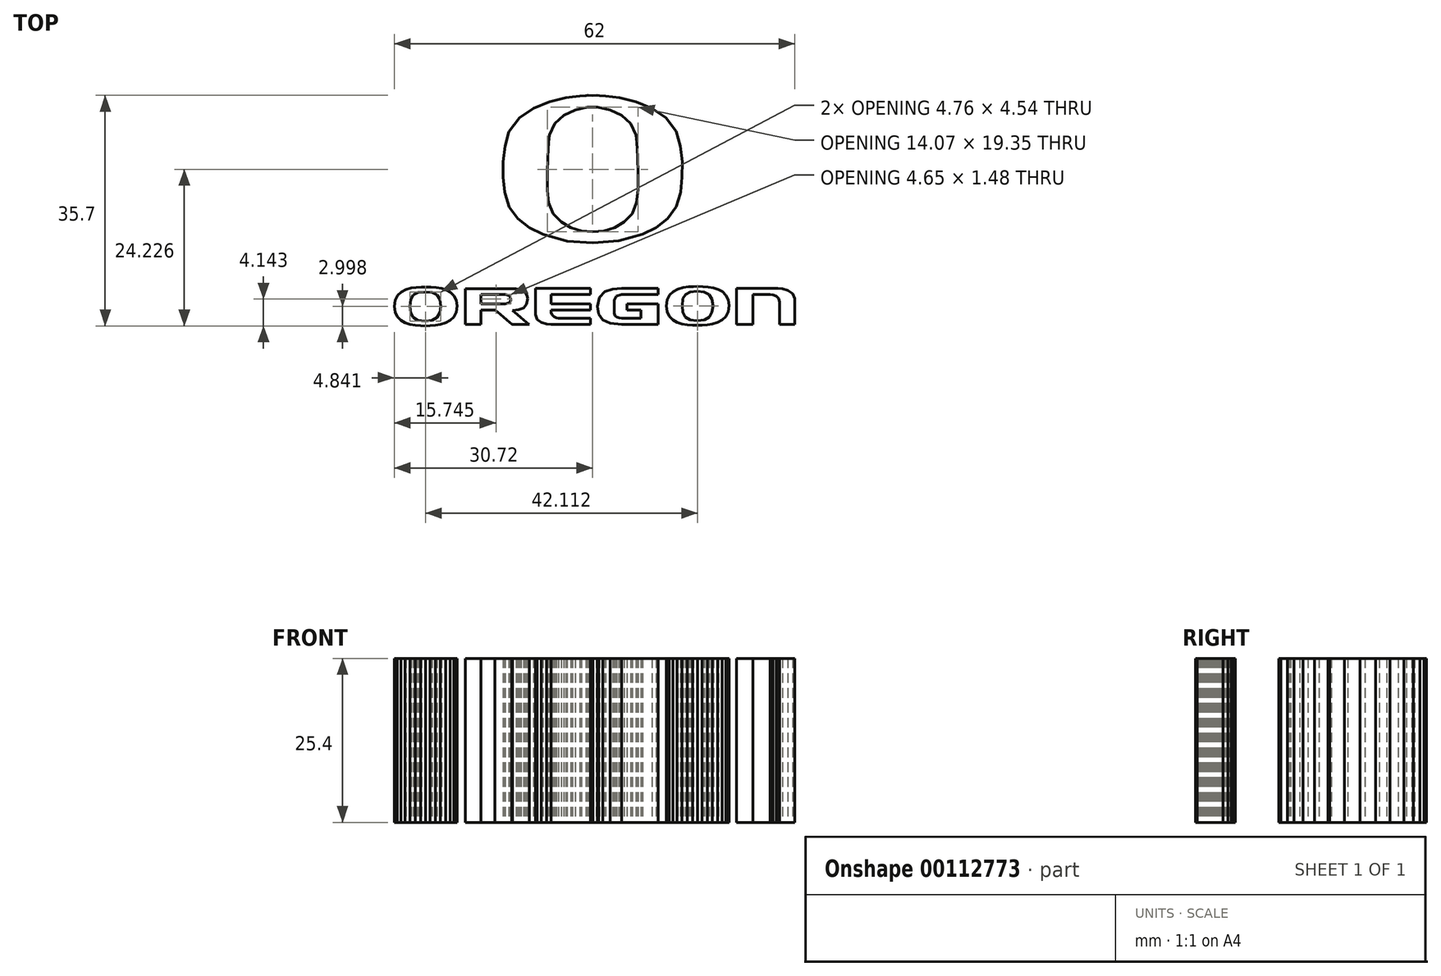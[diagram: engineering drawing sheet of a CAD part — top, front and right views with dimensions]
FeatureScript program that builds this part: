
annotation { "Feature Type Name" : "Feature", "Feature Type Description" : "" }
export const myFeature = defineFeature(function(context is Context, id is Id, definition is map)
    precondition{}
    {
        {
            var Q0;
            Q0=qCreatedBy(makeId("Top.planeOp"),FACE);
            var sketch = newSketch(context, id + "F0", { "sketchPlane" : qUnion([Q0])});
            skLineSegment(sketch, "E0", {"start": v(20.84, -14.7) * mm, "end": v(20.7, -15.65) * mm});
            skLineSegment(sketch, "E1", {"start": v(20.7, -15.65) * mm, "end": v(20.32, -16.38) * mm});
            skLineSegment(sketch, "E2", {"start": v(20.32, -16.38) * mm, "end": v(19.75, -16.93) * mm});
            skLineSegment(sketch, "E3", {"start": v(19.75, -16.93) * mm, "end": v(19.04, -17.3) * mm});
            skLineSegment(sketch, "E4", {"start": v(19.04, -17.3) * mm, "end": v(18.26, -17.56) * mm});
            skLineSegment(sketch, "E5", {"start": v(18.26, -17.56) * mm, "end": v(17.45, -17.7) * mm});
            skLineSegment(sketch, "E6", {"start": v(17.45, -17.7) * mm, "end": v(16.67, -17.76) * mm});
            skLineSegment(sketch, "E7", {"start": v(16.67, -17.76) * mm, "end": v(15.98, -17.78) * mm});
            skLineSegment(sketch, "E8", {"start": v(15.98, -17.78) * mm, "end": v(15.19, -17.76) * mm});
            skLineSegment(sketch, "E9", {"start": v(15.19, -17.76) * mm, "end": v(14.36, -17.68) * mm});
            skLineSegment(sketch, "E10", {"start": v(14.36, -17.68) * mm, "end": v(13.55, -17.53) * mm});
            skLineSegment(sketch, "E11", {"start": v(13.55, -17.53) * mm, "end": v(12.79, -17.28) * mm});
            skLineSegment(sketch, "E12", {"start": v(12.79, -17.28) * mm, "end": v(12.12, -16.9) * mm});
            skLineSegment(sketch, "E13", {"start": v(12.12, -16.9) * mm, "end": v(11.59, -16.36) * mm});
            skLineSegment(sketch, "E14", {"start": v(11.59, -16.36) * mm, "end": v(11.24, -15.66) * mm});
            skLineSegment(sketch, "E15", {"start": v(11.24, -15.66) * mm, "end": v(11.11, -14.76) * mm});
            skLineSegment(sketch, "E16", {"start": v(11.11, -14.76) * mm, "end": v(11.25, -13.79) * mm});
            skLineSegment(sketch, "E17", {"start": v(11.25, -13.79) * mm, "end": v(11.63, -13.05) * mm});
            skLineSegment(sketch, "E18", {"start": v(11.63, -13.05) * mm, "end": v(12.2, -12.52) * mm});
            skLineSegment(sketch, "E19", {"start": v(12.2, -12.52) * mm, "end": v(12.92, -12.15) * mm});
            skLineSegment(sketch, "E20", {"start": v(12.92, -12.15) * mm, "end": v(13.7, -11.92) * mm});
            skLineSegment(sketch, "E21", {"start": v(13.7, -11.92) * mm, "end": v(14.53, -11.8) * mm});
            skLineSegment(sketch, "E22", {"start": v(14.53, -11.8) * mm, "end": v(15.32, -11.75) * mm});
            skLineSegment(sketch, "E23", {"start": v(15.32, -11.75) * mm, "end": v(16.04, -11.74) * mm});
            skLineSegment(sketch, "E24", {"start": v(16.04, -11.74) * mm, "end": v(16.8, -11.76) * mm});
            skLineSegment(sketch, "E25", {"start": v(16.8, -11.76) * mm, "end": v(17.6, -11.82) * mm});
            skLineSegment(sketch, "E26", {"start": v(17.6, -11.82) * mm, "end": v(18.4, -11.96) * mm});
            skLineSegment(sketch, "E27", {"start": v(18.4, -11.96) * mm, "end": v(19.16, -12.2) * mm});
            skLineSegment(sketch, "E28", {"start": v(19.16, -12.2) * mm, "end": v(19.83, -12.56) * mm});
            skLineSegment(sketch, "E29", {"start": v(19.83, -12.56) * mm, "end": v(20.36, -13.08) * mm});
            skLineSegment(sketch, "E30", {"start": v(20.36, -13.08) * mm, "end": v(20.71, -13.79) * mm});
            skLineSegment(sketch, "E31", {"start": v(20.71, -13.79) * mm, "end": v(20.84, -14.7) * mm});
            skLineSegment(sketch, "E32", {"start": v(-0.63, -12.05) * mm, "end": v(-0.63, -12.97) * mm});
            skLineSegment(sketch, "E33", {"start": v(-0.63, -12.97) * mm, "end": v(-6.73, -12.97) * mm});
            skLineSegment(sketch, "E34", {"start": v(-6.73, -12.97) * mm, "end": v(-6.73, -13.2) * mm});
            skLineSegment(sketch, "E35", {"start": v(-6.73, -13.2) * mm, "end": v(-6.73, -13.7) * mm});
            skLineSegment(sketch, "E36", {"start": v(-6.73, -13.7) * mm, "end": v(-6.73, -14.21) * mm});
            skLineSegment(sketch, "E37", {"start": v(-6.73, -14.21) * mm, "end": v(-6.73, -14.45) * mm});
            skLineSegment(sketch, "E38", {"start": v(-6.73, -14.45) * mm, "end": v(-0.63, -14.45) * mm});
            skLineSegment(sketch, "E39", {"start": v(-0.63, -14.45) * mm, "end": v(-0.63, -15.37) * mm});
            skLineSegment(sketch, "E40", {"start": v(-0.63, -15.37) * mm, "end": v(-6.73, -15.37) * mm});
            skLineSegment(sketch, "E41", {"start": v(-6.73, -15.37) * mm, "end": v(-6.74, -15.56) * mm});
            skLineSegment(sketch, "E42", {"start": v(-6.74, -15.56) * mm, "end": v(-6.74, -15.77) * mm});
            skLineSegment(sketch, "E43", {"start": v(-6.74, -15.77) * mm, "end": v(-6.6, -16.1) * mm});
            skLineSegment(sketch, "E44", {"start": v(-6.6, -16.1) * mm, "end": v(-6.27, -16.4) * mm});
            skLineSegment(sketch, "E45", {"start": v(-6.27, -16.4) * mm, "end": v(-5.87, -16.6) * mm});
            skLineSegment(sketch, "E46", {"start": v(-5.87, -16.6) * mm, "end": v(-5.55, -16.67) * mm});
            skLineSegment(sketch, "E47", {"start": v(-5.55, -16.67) * mm, "end": v(-0.63, -16.67) * mm});
            skLineSegment(sketch, "E48", {"start": v(-0.63, -16.67) * mm, "end": v(-0.63, -17.65) * mm});
            skLineSegment(sketch, "E49", {"start": v(-0.63, -17.65) * mm, "end": v(-6.73, -17.65) * mm});
            skLineSegment(sketch, "E50", {"start": v(-6.73, -17.65) * mm, "end": v(-7.45, -17.58) * mm});
            skLineSegment(sketch, "E51", {"start": v(-7.45, -17.58) * mm, "end": v(-8.23, -17.33) * mm});
            skLineSegment(sketch, "E52", {"start": v(-8.23, -17.33) * mm, "end": v(-8.87, -16.85) * mm});
            skLineSegment(sketch, "E53", {"start": v(-8.87, -16.85) * mm, "end": v(-9.13, -16.07) * mm});
            skLineSegment(sketch, "E54", {"start": v(-9.13, -16.07) * mm, "end": v(-9.13, -12.05) * mm});
            skLineSegment(sketch, "E55", {"start": v(-9.13, -12.05) * mm, "end": v(-0.63, -12.05) * mm});
            skLineSegment(sketch, "E56", {"start": v(9.82, -12.05) * mm, "end": v(9.82, -12.97) * mm});
            skLineSegment(sketch, "E57", {"start": v(9.82, -12.97) * mm, "end": v(4.17, -12.97) * mm});
            skLineSegment(sketch, "E58", {"start": v(4.17, -12.97) * mm, "end": v(3.37, -13.2) * mm});
            skLineSegment(sketch, "E59", {"start": v(3.37, -13.2) * mm, "end": v(3.06, -13.9) * mm});
            skLineSegment(sketch, "E60", {"start": v(3.06, -13.9) * mm, "end": v(3.06, -15.9) * mm});
            skLineSegment(sketch, "E61", {"start": v(3.06, -15.9) * mm, "end": v(3.17, -16.27) * mm});
            skLineSegment(sketch, "E62", {"start": v(3.17, -16.27) * mm, "end": v(3.44, -16.5) * mm});
            skLineSegment(sketch, "E63", {"start": v(3.44, -16.5) * mm, "end": v(3.8, -16.63) * mm});
            skLineSegment(sketch, "E64", {"start": v(3.8, -16.63) * mm, "end": v(4.19, -16.67) * mm});
            skLineSegment(sketch, "E65", {"start": v(4.19, -16.67) * mm, "end": v(7.2, -16.67) * mm});
            skLineSegment(sketch, "E66", {"start": v(7.2, -16.67) * mm, "end": v(7.2, -16.46) * mm});
            skLineSegment(sketch, "E67", {"start": v(7.2, -16.46) * mm, "end": v(7.19, -16.01) * mm});
            skLineSegment(sketch, "E68", {"start": v(7.19, -16.01) * mm, "end": v(7.19, -15.56) * mm});
            skLineSegment(sketch, "E69", {"start": v(7.19, -15.56) * mm, "end": v(7.2, -15.37) * mm});
            skLineSegment(sketch, "E70", {"start": v(7.2, -15.37) * mm, "end": v(5.03, -15.37) * mm});
            skLineSegment(sketch, "E71", {"start": v(5.03, -15.37) * mm, "end": v(5.03, -14.45) * mm});
            skLineSegment(sketch, "E72", {"start": v(5.03, -14.45) * mm, "end": v(9.82, -14.45) * mm});
            skLineSegment(sketch, "E73", {"start": v(9.82, -14.45) * mm, "end": v(9.82, -17.65) * mm});
            skLineSegment(sketch, "E74", {"start": v(9.82, -17.65) * mm, "end": v(4.19, -17.65) * mm});
            skLineSegment(sketch, "E75", {"start": v(4.19, -17.65) * mm, "end": v(2.4, -17.45) * mm});
            skLineSegment(sketch, "E76", {"start": v(2.4, -17.45) * mm, "end": v(1.27, -16.9) * mm});
            skLineSegment(sketch, "E77", {"start": v(1.27, -16.9) * mm, "end": v(0.66, -16) * mm});
            skLineSegment(sketch, "E78", {"start": v(0.66, -16) * mm, "end": v(0.48, -14.82) * mm});
            skLineSegment(sketch, "E79", {"start": v(0.48, -14.82) * mm, "end": v(0.79, -13.4) * mm});
            skLineSegment(sketch, "E80", {"start": v(0.79, -13.4) * mm, "end": v(1.61, -12.56) * mm});
            skLineSegment(sketch, "E81", {"start": v(1.61, -12.56) * mm, "end": v(2.8, -12.15) * mm});
            skLineSegment(sketch, "E82", {"start": v(2.8, -12.15) * mm, "end": v(4.19, -12.05) * mm});
            skLineSegment(sketch, "E83", {"start": v(4.19, -12.05) * mm, "end": v(9.82, -12.05) * mm});
            skLineSegment(sketch, "E84", {"start": v(28.4, -12.05) * mm, "end": v(29.08, -12.11) * mm});
            skLineSegment(sketch, "E85", {"start": v(29.08, -12.11) * mm, "end": v(29.94, -12.36) * mm});
            skLineSegment(sketch, "E86", {"start": v(29.94, -12.36) * mm, "end": v(30.68, -12.83) * mm});
            skLineSegment(sketch, "E87", {"start": v(30.68, -12.83) * mm, "end": v(31, -13.6) * mm});
            skLineSegment(sketch, "E88", {"start": v(31, -13.6) * mm, "end": v(31, -17.65) * mm});
            skLineSegment(sketch, "E89", {"start": v(31, -17.65) * mm, "end": v(28.66, -17.65) * mm});
            skLineSegment(sketch, "E90", {"start": v(28.66, -17.65) * mm, "end": v(28.66, -14.19) * mm});
            skLineSegment(sketch, "E91", {"start": v(28.66, -14.19) * mm, "end": v(28.5, -13.63) * mm});
            skLineSegment(sketch, "E92", {"start": v(28.5, -13.63) * mm, "end": v(28.11, -13.25) * mm});
            skLineSegment(sketch, "E93", {"start": v(28.11, -13.25) * mm, "end": v(27.64, -13.04) * mm});
            skLineSegment(sketch, "E94", {"start": v(27.64, -13.04) * mm, "end": v(27.2, -12.97) * mm});
            skLineSegment(sketch, "E95", {"start": v(27.2, -12.97) * mm, "end": v(24.53, -12.97) * mm});
            skLineSegment(sketch, "E96", {"start": v(24.53, -12.97) * mm, "end": v(24.53, -17.65) * mm});
            skLineSegment(sketch, "E97", {"start": v(24.53, -17.65) * mm, "end": v(22.01, -17.65) * mm});
            skLineSegment(sketch, "E98", {"start": v(22.01, -17.65) * mm, "end": v(22.01, -12.05) * mm});
            skLineSegment(sketch, "E99", {"start": v(22.01, -12.05) * mm, "end": v(28.4, -12.05) * mm});
            skLineSegment(sketch, "E100", {"start": v(-12.1, -12.11) * mm, "end": v(-11.36, -12.22) * mm});
            skLineSegment(sketch, "E101", {"start": v(-11.36, -12.22) * mm, "end": v(-10.8, -12.54) * mm});
            skLineSegment(sketch, "E102", {"start": v(-10.8, -12.54) * mm, "end": v(-10.47, -13.03) * mm});
            skLineSegment(sketch, "E103", {"start": v(-10.47, -13.03) * mm, "end": v(-10.36, -13.65) * mm});
            skLineSegment(sketch, "E104", {"start": v(-10.36, -13.65) * mm, "end": v(-10.52, -14.52) * mm});
            skLineSegment(sketch, "E105", {"start": v(-10.52, -14.52) * mm, "end": v(-10.97, -15.06) * mm});
            skLineSegment(sketch, "E106", {"start": v(-10.97, -15.06) * mm, "end": v(-11.7, -15.35) * mm});
            skLineSegment(sketch, "E107", {"start": v(-11.7, -15.35) * mm, "end": v(-12.72, -15.43) * mm});
            skLineSegment(sketch, "E108", {"start": v(-12.72, -15.43) * mm, "end": v(-12.61, -15.52) * mm});
            skLineSegment(sketch, "E109", {"start": v(-12.61, -15.52) * mm, "end": v(-12.32, -15.77) * mm});
            skLineSegment(sketch, "E110", {"start": v(-12.32, -15.77) * mm, "end": v(-11.9, -16.13) * mm});
            skLineSegment(sketch, "E111", {"start": v(-11.9, -16.13) * mm, "end": v(-11.42, -16.54) * mm});
            skLineSegment(sketch, "E112", {"start": v(-11.42, -16.54) * mm, "end": v(-10.94, -16.94) * mm});
            skLineSegment(sketch, "E113", {"start": v(-10.94, -16.94) * mm, "end": v(-10.52, -17.3) * mm});
            skLineSegment(sketch, "E114", {"start": v(-10.52, -17.3) * mm, "end": v(-10.23, -17.55) * mm});
            skLineSegment(sketch, "E115", {"start": v(-10.23, -17.55) * mm, "end": v(-10.11, -17.65) * mm});
            skLineSegment(sketch, "E116", {"start": v(-10.11, -17.65) * mm, "end": v(-10.77, -17.65) * mm});
            skLineSegment(sketch, "E117", {"start": v(-10.77, -17.65) * mm, "end": v(-12.72, -17.65) * mm});
            skLineSegment(sketch, "E118", {"start": v(-12.72, -17.65) * mm, "end": v(-12.83, -17.55) * mm});
            skLineSegment(sketch, "E119", {"start": v(-12.83, -17.55) * mm, "end": v(-13.14, -17.3) * mm});
            skLineSegment(sketch, "E120", {"start": v(-13.14, -17.3) * mm, "end": v(-13.57, -16.92) * mm});
            skLineSegment(sketch, "E121", {"start": v(-13.57, -16.92) * mm, "end": v(-14.06, -16.5) * mm});
            skLineSegment(sketch, "E122", {"start": v(-14.06, -16.5) * mm, "end": v(-14.56, -16.09) * mm});
            skLineSegment(sketch, "E123", {"start": v(-14.56, -16.09) * mm, "end": v(-14.99, -15.72) * mm});
            skLineSegment(sketch, "E124", {"start": v(-14.99, -15.72) * mm, "end": v(-15.3, -15.47) * mm});
            skLineSegment(sketch, "E125", {"start": v(-15.3, -15.47) * mm, "end": v(-15.4, -15.37) * mm});
            skLineSegment(sketch, "E126", {"start": v(-15.4, -15.37) * mm, "end": v(-17.58, -15.37) * mm});
            skLineSegment(sketch, "E127", {"start": v(-17.58, -15.37) * mm, "end": v(-17.58, -17.65) * mm});
            skLineSegment(sketch, "E128", {"start": v(-17.58, -17.65) * mm, "end": v(-19.96, -17.65) * mm});
            skLineSegment(sketch, "E129", {"start": v(-19.96, -17.65) * mm, "end": v(-19.96, -12.11) * mm});
            skLineSegment(sketch, "E130", {"start": v(-19.96, -12.11) * mm, "end": v(-12.1, -12.11) * mm});
            skLineSegment(sketch, "E131", {"start": v(13.57, -14.76) * mm, "end": v(13.7, -15.74) * mm});
            skLineSegment(sketch, "E132", {"start": v(13.7, -15.74) * mm, "end": v(14.07, -16.46) * mm});
            skLineSegment(sketch, "E133", {"start": v(14.07, -16.46) * mm, "end": v(14.78, -16.9) * mm});
            skLineSegment(sketch, "E134", {"start": v(14.78, -16.9) * mm, "end": v(15.87, -17.05) * mm});
            skLineSegment(sketch, "E135", {"start": v(15.87, -17.05) * mm, "end": v(17, -16.9) * mm});
            skLineSegment(sketch, "E136", {"start": v(17, -16.9) * mm, "end": v(17.76, -16.46) * mm});
            skLineSegment(sketch, "E137", {"start": v(17.76, -16.46) * mm, "end": v(18.2, -15.73) * mm});
            skLineSegment(sketch, "E138", {"start": v(18.2, -15.73) * mm, "end": v(18.33, -14.74) * mm});
            skLineSegment(sketch, "E139", {"start": v(18.33, -14.74) * mm, "end": v(18.2, -13.65) * mm});
            skLineSegment(sketch, "E140", {"start": v(18.2, -13.65) * mm, "end": v(17.76, -12.97) * mm});
            skLineSegment(sketch, "E141", {"start": v(17.76, -12.97) * mm, "end": v(17, -12.61) * mm});
            skLineSegment(sketch, "E142", {"start": v(17, -12.61) * mm, "end": v(15.87, -12.5) * mm});
            skLineSegment(sketch, "E143", {"start": v(15.87, -12.5) * mm, "end": v(14.8, -12.6) * mm});
            skLineSegment(sketch, "E144", {"start": v(14.8, -12.6) * mm, "end": v(14.08, -12.96) * mm});
            skLineSegment(sketch, "E145", {"start": v(14.08, -12.96) * mm, "end": v(13.7, -13.65) * mm});
            skLineSegment(sketch, "E146", {"start": v(13.7, -13.65) * mm, "end": v(13.57, -14.76) * mm});
            skLineSegment(sketch, "E147", {"start": v(-17.58, -14.45) * mm, "end": v(-17.42, -14.44) * mm});
            skLineSegment(sketch, "E148", {"start": v(-17.42, -14.44) * mm, "end": v(-17, -14.44) * mm});
            skLineSegment(sketch, "E149", {"start": v(-17, -14.44) * mm, "end": v(-16.4, -14.44) * mm});
            skLineSegment(sketch, "E150", {"start": v(-16.4, -14.44) * mm, "end": v(-15.7, -14.44) * mm});
            skLineSegment(sketch, "E151", {"start": v(-15.7, -14.44) * mm, "end": v(-15.02, -14.44) * mm});
            skLineSegment(sketch, "E152", {"start": v(-15.02, -14.44) * mm, "end": v(-14.42, -14.44) * mm});
            skLineSegment(sketch, "E153", {"start": v(-14.42, -14.44) * mm, "end": v(-14, -14.44) * mm});
            skLineSegment(sketch, "E154", {"start": v(-14, -14.44) * mm, "end": v(-13.84, -14.45) * mm});
            skLineSegment(sketch, "E155", {"start": v(-13.84, -14.45) * mm, "end": v(-13.16, -14.29) * mm});
            skLineSegment(sketch, "E156", {"start": v(-13.16, -14.29) * mm, "end": v(-12.93, -13.78) * mm});
            skLineSegment(sketch, "E157", {"start": v(-12.93, -13.78) * mm, "end": v(-13.14, -13.2) * mm});
            skLineSegment(sketch, "E158", {"start": v(-13.14, -13.2) * mm, "end": v(-13.82, -12.97) * mm});
            skLineSegment(sketch, "E159", {"start": v(-13.82, -12.97) * mm, "end": v(-17.58, -12.97) * mm});
            skLineSegment(sketch, "E160", {"start": v(-17.58, -12.97) * mm, "end": v(-17.58, -14.45) * mm});
            skLineSegment(sketch, "E161", {"start": v(-21.27, -14.77) * mm, "end": v(-21.41, -15.73) * mm});
            skLineSegment(sketch, "E162", {"start": v(-21.41, -15.73) * mm, "end": v(-21.8, -16.46) * mm});
            skLineSegment(sketch, "E163", {"start": v(-21.8, -16.46) * mm, "end": v(-22.36, -17) * mm});
            skLineSegment(sketch, "E164", {"start": v(-22.36, -17) * mm, "end": v(-23.07, -17.39) * mm});
            skLineSegment(sketch, "E165", {"start": v(-23.07, -17.39) * mm, "end": v(-23.85, -17.63) * mm});
            skLineSegment(sketch, "E166", {"start": v(-23.85, -17.63) * mm, "end": v(-24.66, -17.77) * mm});
            skLineSegment(sketch, "E167", {"start": v(-24.66, -17.77) * mm, "end": v(-25.44, -17.84) * mm});
            skLineSegment(sketch, "E168", {"start": v(-25.44, -17.84) * mm, "end": v(-26.14, -17.85) * mm});
            skLineSegment(sketch, "E169", {"start": v(-26.14, -17.85) * mm, "end": v(-26.92, -17.83) * mm});
            skLineSegment(sketch, "E170", {"start": v(-26.92, -17.83) * mm, "end": v(-27.75, -17.76) * mm});
            skLineSegment(sketch, "E171", {"start": v(-27.75, -17.76) * mm, "end": v(-28.56, -17.6) * mm});
            skLineSegment(sketch, "E172", {"start": v(-28.56, -17.6) * mm, "end": v(-29.32, -17.35) * mm});
            skLineSegment(sketch, "E173", {"start": v(-29.32, -17.35) * mm, "end": v(-30, -16.97) * mm});
            skLineSegment(sketch, "E174", {"start": v(-30, -16.97) * mm, "end": v(-30.52, -16.44) * mm});
            skLineSegment(sketch, "E175", {"start": v(-30.52, -16.44) * mm, "end": v(-30.87, -15.74) * mm});
            skLineSegment(sketch, "E176", {"start": v(-30.87, -15.74) * mm, "end": v(-31, -14.83) * mm});
            skLineSegment(sketch, "E177", {"start": v(-31, -14.83) * mm, "end": v(-30.86, -13.86) * mm});
            skLineSegment(sketch, "E178", {"start": v(-30.86, -13.86) * mm, "end": v(-30.48, -13.13) * mm});
            skLineSegment(sketch, "E179", {"start": v(-30.48, -13.13) * mm, "end": v(-29.9, -12.6) * mm});
            skLineSegment(sketch, "E180", {"start": v(-29.9, -12.6) * mm, "end": v(-29.2, -12.23) * mm});
            skLineSegment(sketch, "E181", {"start": v(-29.2, -12.23) * mm, "end": v(-28.4, -12) * mm});
            skLineSegment(sketch, "E182", {"start": v(-28.4, -12) * mm, "end": v(-27.59, -11.88) * mm});
            skLineSegment(sketch, "E183", {"start": v(-27.59, -11.88) * mm, "end": v(-26.8, -11.82) * mm});
            skLineSegment(sketch, "E184", {"start": v(-26.8, -11.82) * mm, "end": v(-26.08, -11.82) * mm});
            skLineSegment(sketch, "E185", {"start": v(-26.08, -11.82) * mm, "end": v(-25.31, -11.83) * mm});
            skLineSegment(sketch, "E186", {"start": v(-25.31, -11.83) * mm, "end": v(-24.5, -11.9) * mm});
            skLineSegment(sketch, "E187", {"start": v(-24.5, -11.9) * mm, "end": v(-23.7, -12.03) * mm});
            skLineSegment(sketch, "E188", {"start": v(-23.7, -12.03) * mm, "end": v(-22.95, -12.27) * mm});
            skLineSegment(sketch, "E189", {"start": v(-22.95, -12.27) * mm, "end": v(-22.28, -12.64) * mm});
            skLineSegment(sketch, "E190", {"start": v(-22.28, -12.64) * mm, "end": v(-21.75, -13.16) * mm});
            skLineSegment(sketch, "E191", {"start": v(-21.75, -13.16) * mm, "end": v(-21.4, -13.86) * mm});
            skLineSegment(sketch, "E192", {"start": v(-21.4, -13.86) * mm, "end": v(-21.27, -14.77) * mm});
            skLineSegment(sketch, "E193", {"start": v(-28.54, -14.83) * mm, "end": v(-28.42, -15.82) * mm});
            skLineSegment(sketch, "E194", {"start": v(-28.42, -15.82) * mm, "end": v(-28.04, -16.54) * mm});
            skLineSegment(sketch, "E195", {"start": v(-28.04, -16.54) * mm, "end": v(-27.33, -16.97) * mm});
            skLineSegment(sketch, "E196", {"start": v(-27.33, -16.97) * mm, "end": v(-26.24, -17.12) * mm});
            skLineSegment(sketch, "E197", {"start": v(-26.24, -17.12) * mm, "end": v(-25.11, -16.97) * mm});
            skLineSegment(sketch, "E198", {"start": v(-25.11, -16.97) * mm, "end": v(-24.35, -16.53) * mm});
            skLineSegment(sketch, "E199", {"start": v(-24.35, -16.53) * mm, "end": v(-23.92, -15.81) * mm});
            skLineSegment(sketch, "E200", {"start": v(-23.92, -15.81) * mm, "end": v(-23.78, -14.81) * mm});
            skLineSegment(sketch, "E201", {"start": v(-23.78, -14.81) * mm, "end": v(-23.92, -13.73) * mm});
            skLineSegment(sketch, "E202", {"start": v(-23.92, -13.73) * mm, "end": v(-24.36, -13.04) * mm});
            skLineSegment(sketch, "E203", {"start": v(-24.36, -13.04) * mm, "end": v(-25.12, -12.68) * mm});
            skLineSegment(sketch, "E204", {"start": v(-25.12, -12.68) * mm, "end": v(-26.24, -12.58) * mm});
            skLineSegment(sketch, "E205", {"start": v(-26.24, -12.58) * mm, "end": v(-27.32, -12.68) * mm});
            skLineSegment(sketch, "E206", {"start": v(-27.32, -12.68) * mm, "end": v(-28.03, -13.04) * mm});
            skLineSegment(sketch, "E207", {"start": v(-28.03, -13.04) * mm, "end": v(-28.42, -13.73) * mm});
            skLineSegment(sketch, "E208", {"start": v(-28.42, -13.73) * mm, "end": v(-28.54, -14.83) * mm});
            skLineSegment(sketch, "E209", {"start": v(12.68, 12.26) * mm, "end": v(11.05, 14.39) * mm});
            skLineSegment(sketch, "E210", {"start": v(11.05, 14.39) * mm, "end": v(8.9, 15.86) * mm});
            skLineSegment(sketch, "E211", {"start": v(8.9, 15.86) * mm, "end": v(6.44, 16.84) * mm});
            skLineSegment(sketch, "E212", {"start": v(6.44, 16.84) * mm, "end": v(3.86, 17.48) * mm});
            skLineSegment(sketch, "E213", {"start": v(3.86, 17.48) * mm, "end": v(2.83, 17.65) * mm});
            skLineSegment(sketch, "E214", {"start": v(2.83, 17.65) * mm, "end": v(1.7, 17.76) * mm});
            skLineSegment(sketch, "E215", {"start": v(1.7, 17.76) * mm, "end": v(0.79, 17.83) * mm});
            skLineSegment(sketch, "E216", {"start": v(0.79, 17.83) * mm, "end": v(0.42, 17.85) * mm});
            skLineSegment(sketch, "E217", {"start": v(0.42, 17.85) * mm, "end": v(-0.28, 17.84) * mm});
            skLineSegment(sketch, "E218", {"start": v(-0.28, 17.84) * mm, "end": v(-0.28, 17.83) * mm});
            skLineSegment(sketch, "E219", {"start": v(-0.28, 17.83) * mm, "end": v(-0.98, 17.85) * mm});
            skLineSegment(sketch, "E220", {"start": v(-0.98, 17.85) * mm, "end": v(-1.35, 17.82) * mm});
            skLineSegment(sketch, "E221", {"start": v(-1.35, 17.82) * mm, "end": v(-2.26, 17.76) * mm});
            skLineSegment(sketch, "E222", {"start": v(-2.26, 17.76) * mm, "end": v(-3.4, 17.64) * mm});
            skLineSegment(sketch, "E223", {"start": v(-3.4, 17.64) * mm, "end": v(-4.42, 17.47) * mm});
            skLineSegment(sketch, "E224", {"start": v(-4.42, 17.47) * mm, "end": v(-7, 16.83) * mm});
            skLineSegment(sketch, "E225", {"start": v(-7, 16.83) * mm, "end": v(-9.46, 15.85) * mm});
            skLineSegment(sketch, "E226", {"start": v(-9.46, 15.85) * mm, "end": v(-11.62, 14.38) * mm});
            skLineSegment(sketch, "E227", {"start": v(-11.62, 14.38) * mm, "end": v(-13.24, 12.25) * mm});
            skLineSegment(sketch, "E228", {"start": v(-13.24, 12.25) * mm, "end": v(-13.86, 10) * mm});
            skLineSegment(sketch, "E229", {"start": v(-13.86, 10) * mm, "end": v(-14.14, 7.58) * mm});
            skLineSegment(sketch, "E230", {"start": v(-14.14, 7.58) * mm, "end": v(-14.13, 5.16) * mm});
            skLineSegment(sketch, "E231", {"start": v(-14.13, 5.16) * mm, "end": v(-13.9, 2.88) * mm});
            skLineSegment(sketch, "E232", {"start": v(-13.9, 2.88) * mm, "end": v(-13.86, 2.64) * mm});
            skLineSegment(sketch, "E233", {"start": v(-13.86, 2.64) * mm, "end": v(-13.2, 0.57) * mm});
            skLineSegment(sketch, "E234", {"start": v(-13.2, 0.57) * mm, "end": v(-11.89, -1.22) * mm});
            skLineSegment(sketch, "E235", {"start": v(-11.89, -1.22) * mm, "end": v(-10.1, -2.65) * mm});
            skLineSegment(sketch, "E236", {"start": v(-10.1, -2.65) * mm, "end": v(-8.01, -3.64) * mm});
            skLineSegment(sketch, "E237", {"start": v(-8.01, -3.64) * mm, "end": v(-4.27, -4.7) * mm});
            skLineSegment(sketch, "E238", {"start": v(-4.27, -4.7) * mm, "end": v(-0.25, -4.99) * mm});
            skLineSegment(sketch, "E239", {"start": v(-0.25, -4.99) * mm, "end": v(-0.25, -4.98) * mm});
            skLineSegment(sketch, "E240", {"start": v(-0.25, -4.98) * mm, "end": v(3.74, -4.7) * mm});
            skLineSegment(sketch, "E241", {"start": v(3.74, -4.7) * mm, "end": v(7.45, -3.63) * mm});
            skLineSegment(sketch, "E242", {"start": v(7.45, -3.63) * mm, "end": v(9.54, -2.64) * mm});
            skLineSegment(sketch, "E243", {"start": v(9.54, -2.64) * mm, "end": v(11.33, -1.21) * mm});
            skLineSegment(sketch, "E244", {"start": v(11.33, -1.21) * mm, "end": v(12.64, 0.57) * mm});
            skLineSegment(sketch, "E245", {"start": v(12.64, 0.57) * mm, "end": v(13.3, 2.64) * mm});
            skLineSegment(sketch, "E246", {"start": v(13.3, 2.64) * mm, "end": v(13.33, 2.88) * mm});
            skLineSegment(sketch, "E247", {"start": v(13.33, 2.88) * mm, "end": v(13.57, 5.16) * mm});
            skLineSegment(sketch, "E248", {"start": v(13.57, 5.16) * mm, "end": v(13.58, 7.59) * mm});
            skLineSegment(sketch, "E249", {"start": v(13.58, 7.59) * mm, "end": v(13.3, 10) * mm});
            skLineSegment(sketch, "E250", {"start": v(13.3, 10) * mm, "end": v(12.68, 12.26) * mm});
            skLineSegment(sketch, "E251", {"start": v(6.71, 3.18) * mm, "end": v(6.5, 1.27) * mm});
            skLineSegment(sketch, "E252", {"start": v(6.5, 1.27) * mm, "end": v(5.85, -0.47) * mm});
            skLineSegment(sketch, "E253", {"start": v(5.85, -0.47) * mm, "end": v(4.59, -1.74) * mm});
            skLineSegment(sketch, "E254", {"start": v(4.59, -1.74) * mm, "end": v(3.1, -2.61) * mm});
            skLineSegment(sketch, "E255", {"start": v(3.1, -2.61) * mm, "end": v(1.45, -3.12) * mm});
            skLineSegment(sketch, "E256", {"start": v(1.45, -3.12) * mm, "end": v(-0.28, -3.3) * mm});
            skLineSegment(sketch, "E257", {"start": v(-0.28, -3.3) * mm, "end": v(-0.28, -3.3) * mm});
            skLineSegment(sketch, "E258", {"start": v(-0.28, -3.3) * mm, "end": v(-2.01, -3.13) * mm});
            skLineSegment(sketch, "E259", {"start": v(-2.01, -3.13) * mm, "end": v(-3.66, -2.62) * mm});
            skLineSegment(sketch, "E260", {"start": v(-3.66, -2.62) * mm, "end": v(-5.15, -1.74) * mm});
            skLineSegment(sketch, "E261", {"start": v(-5.15, -1.74) * mm, "end": v(-6.4, -0.48) * mm});
            skLineSegment(sketch, "E262", {"start": v(-6.4, -0.48) * mm, "end": v(-7.07, 1.26) * mm});
            skLineSegment(sketch, "E263", {"start": v(-7.07, 1.26) * mm, "end": v(-7.27, 3.17) * mm});
            skLineSegment(sketch, "E264", {"start": v(-7.27, 3.17) * mm, "end": v(-7.32, 5.67) * mm});
            skLineSegment(sketch, "E265", {"start": v(-7.32, 5.67) * mm, "end": v(-7.25, 8.34) * mm});
            skLineSegment(sketch, "E266", {"start": v(-7.25, 8.34) * mm, "end": v(-7.13, 10.57) * mm});
            skLineSegment(sketch, "E267", {"start": v(-7.13, 10.57) * mm, "end": v(-7, 11.72) * mm});
            skLineSegment(sketch, "E268", {"start": v(-7, 11.72) * mm, "end": v(-6.14, 13.47) * mm});
            skLineSegment(sketch, "E269", {"start": v(-6.14, 13.47) * mm, "end": v(-4.74, 14.77) * mm});
            skLineSegment(sketch, "E270", {"start": v(-4.74, 14.77) * mm, "end": v(-3, 15.6) * mm});
            skLineSegment(sketch, "E271", {"start": v(-3, 15.6) * mm, "end": v(-1.04, 16) * mm});
            skLineSegment(sketch, "E272", {"start": v(-1.04, 16) * mm, "end": v(-0.78, 16.03) * mm});
            skLineSegment(sketch, "E273", {"start": v(-0.78, 16.03) * mm, "end": v(-0.25, 16.05) * mm});
            skLineSegment(sketch, "E274", {"start": v(-0.25, 16.05) * mm, "end": v(-0.25, 16.05) * mm});
            skLineSegment(sketch, "E275", {"start": v(-0.25, 16.05) * mm, "end": v(0.24, 16.03) * mm});
            skLineSegment(sketch, "E276", {"start": v(0.24, 16.03) * mm, "end": v(0.48, 16.01) * mm});
            skLineSegment(sketch, "E277", {"start": v(0.48, 16.01) * mm, "end": v(2.43, 15.61) * mm});
            skLineSegment(sketch, "E278", {"start": v(2.43, 15.61) * mm, "end": v(4.18, 14.77) * mm});
            skLineSegment(sketch, "E279", {"start": v(4.18, 14.77) * mm, "end": v(5.57, 13.48) * mm});
            skLineSegment(sketch, "E280", {"start": v(5.57, 13.48) * mm, "end": v(6.44, 11.72) * mm});
            skLineSegment(sketch, "E281", {"start": v(6.44, 11.72) * mm, "end": v(6.57, 10.57) * mm});
            skLineSegment(sketch, "E282", {"start": v(6.57, 10.57) * mm, "end": v(6.7, 8.35) * mm});
            skLineSegment(sketch, "E283", {"start": v(6.7, 8.35) * mm, "end": v(6.76, 5.67) * mm});
            skLineSegment(sketch, "E284", {"start": v(6.76, 5.67) * mm, "end": v(6.71, 3.18) * mm});
            skSolve(sketch);
        }
        {
            var Q0;
            Q0=makeQuery(id+"F0.imprint","IMPRINT",FACE,{"disambiguationData":[TD([[makeQuery(id+"F0.imprint","IMPRINT",EDGE,{"derivedFrom":sQuery(id+"F0.wireOp",EDGE,"E209")}),1.0]])]});
            var Q1;
            Q1=makeQuery(id+"F0.imprint","IMPRINT",FACE,{"disambiguationData":[TD([[makeQuery(id+"F0.imprint","IMPRINT",EDGE,{"derivedFrom":sQuery(id+"F0.wireOp",EDGE,"E161")}),-1.0]])]});
            var Q2;
            Q2=makeQuery(id+"F0.imprint","IMPRINT",FACE,{"disambiguationData":[TD([[makeQuery(id+"F0.imprint","IMPRINT",EDGE,{"derivedFrom":sQuery(id+"F0.wireOp",EDGE,"E100")}),-1.0]])]});
            var Q3;
            Q3=makeQuery(id+"F0.imprint","IMPRINT",FACE,{"disambiguationData":[TD([[makeQuery(id+"F0.imprint","IMPRINT",EDGE,{"derivedFrom":sQuery(id+"F0.wireOp",EDGE,"E56")}),-1.0]])]});
            var Q4;
            Q4=makeQuery(id+"F0.imprint","IMPRINT",FACE,{"disambiguationData":[TD([[makeQuery(id+"F0.imprint","IMPRINT",EDGE,{"derivedFrom":sQuery(id+"F0.wireOp",EDGE,"E32")}),-1.0]])]});
            var Q5;
            Q5=makeQuery(id+"F0.imprint","IMPRINT",FACE,{"disambiguationData":[TD([[makeQuery(id+"F0.imprint","IMPRINT",EDGE,{"derivedFrom":sQuery(id+"F0.wireOp",EDGE,"E0")}),-1.0]])]});
            var Q6;
            Q6=makeQuery(id+"F0.imprint","IMPRINT",FACE,{"disambiguationData":[TD([[makeQuery(id+"F0.imprint","IMPRINT",EDGE,{"derivedFrom":sQuery(id+"F0.wireOp",EDGE,"E84")}),-1.0]])]});
            extrude(context, id + "F1", {"entities" : qUnion([Q0, Q1, Q2, Q3, Q4, Q5, Q6]), "depth" : 25.4 * mm});
        }
    });
